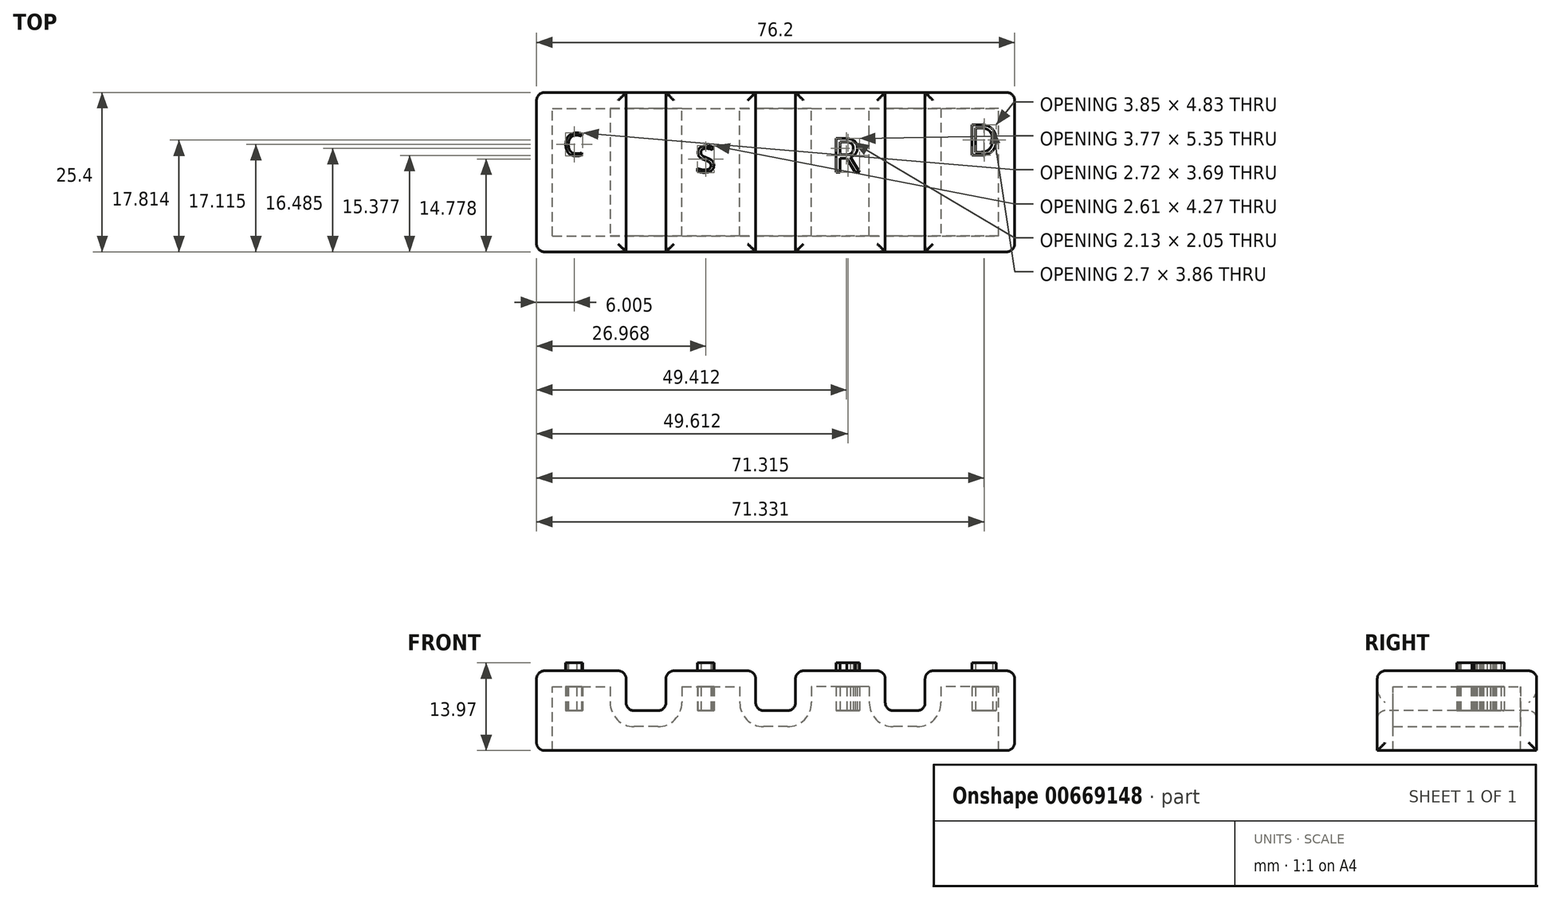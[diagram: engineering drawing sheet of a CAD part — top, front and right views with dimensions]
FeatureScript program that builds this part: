
annotation { "Feature Type Name" : "Feature", "Feature Type Description" : "" }
export const myFeature = defineFeature(function(context is Context, id is Id, definition is map)
    precondition{}
    {
        {
            var Q0;
            Q0=qCreatedBy(makeId("Top.planeOp"),FACE);
            var sketch = newSketch(context, id + "F0", { "sketchPlane" : qUnion([Q0])});
            skLineSegment(sketch, "E0.bottom", {"start": v(-38.1, 12.7) * mm, "end": v(38.1, 12.7) * mm});
            skLineSegment(sketch, "E0.top", {"start": v(-38.1, -12.7) * mm, "end": v(38.1, -12.7) * mm});
            skLineSegment(sketch, "E0.left", {"start": v(-38.1, 12.7) * mm, "end": v(-38.1, -12.7) * mm});
            skLineSegment(sketch, "E0.right", {"start": v(38.1, 12.7) * mm, "end": v(38.1, -12.7) * mm});
            skPoint(sketch, "E0.middle", {"position": v(0, 0) * mm});
            skSolve(sketch);
        }
        {
            var Q0;
            Q0 = qSketchRegion(id + "F0", true);
            extrude(context, id + "F1", {"entities" : qUnion([Q0]), "depth" : 12.7 * mm, "offsetDistance" : 25.4 * mm});
        }
        {
            var Q0;
            Q0=makeQuery(id+"F1.opExtrude","SWEPT_FACE",FACE,{"disambiguationData":[OSD([sQuery(id+"F0.wireOp",EDGE,"E0.top")])]});
            var sketch = newSketch(context, id + "F2", { "sketchPlane" : qUnion([Q0])});
            skLineSegment(sketch, "E1", {"start": v(-38.1, 6.35) * mm, "end": v(38.1, 6.35) * mm, "construction": true});
            skLineSegment(sketch, "E2.bottom", {"start": v(-3.18, 6.35) * mm, "end": v(3.17, 6.35) * mm});
            skLineSegment(sketch, "E2.top", {"start": v(-3.18, 19.05) * mm, "end": v(3.17, 19.05) * mm});
            skLineSegment(sketch, "E2.left", {"start": v(-3.18, 6.35) * mm, "end": v(-3.18, 19.05) * mm});
            skLineSegment(sketch, "E2.right", {"start": v(3.17, 6.35) * mm, "end": v(3.17, 19.05) * mm});
            skPoint(sketch, "E2.middle", {"position": v(0, 12.7) * mm});
            skLineSegment(sketch, "E3.bottom", {"start": v(-23.83, 6.35) * mm, "end": v(-17.48, 6.35) * mm});
            skLineSegment(sketch, "E3.top", {"start": v(-23.83, 19.05) * mm, "end": v(-17.48, 19.05) * mm});
            skLineSegment(sketch, "E3.left", {"start": v(-23.83, 6.35) * mm, "end": v(-23.83, 19.05) * mm});
            skLineSegment(sketch, "E3.right", {"start": v(-17.48, 6.35) * mm, "end": v(-17.48, 19.05) * mm});
            skPoint(sketch, "E3.middle", {"position": v(-20.65, 12.7) * mm});
            skLineSegment(sketch, "E4.bottom", {"start": v(17.48, 6.35) * mm, "end": v(23.83, 6.35) * mm});
            skLineSegment(sketch, "E4.top", {"start": v(17.48, 19.05) * mm, "end": v(23.83, 19.05) * mm});
            skLineSegment(sketch, "E4.left", {"start": v(17.48, 6.35) * mm, "end": v(17.48, 19.05) * mm});
            skLineSegment(sketch, "E4.right", {"start": v(23.83, 6.35) * mm, "end": v(23.83, 19.05) * mm});
            skPoint(sketch, "E4.middle", {"position": v(20.65, 12.7) * mm});
            skSolve(sketch);
        }
        {
            var Q0;
            Q0 = qSketchRegion(id + "F2", true);
            extrude(context, id + "F3", {"entities" : qUnion([Q0]), "operationType" : NewBodyOperationType.REMOVE, "endBound" : BoundingType.THROUGH_ALL, "oppositeDirection" : true, "depth" : 25.4 * mm, "offsetDistance" : 25.4 * mm});
        }
        {
            var Q0;
            {var subQ0=sQuery(id+"F0.wireOp",EDGE,"E0.bottom");var subQ1=sQuery(id+"F0.wireOp",EDGE,"E0.top");var subQ2=sQuery(id+"F0.wireOp",EDGE,"E0.left");Q0=makeQuery(id+"F3.boolean.opBoolean","SPLIT",FACE,{"disambiguationData":[TD([makeQuery(id+"F1.opExtrude","SWEPT_FACE",FACE,{"disambiguationData":[OSD([subQ2])]})])],"derivedFrom":makeQuery(id+"F1.opExtrude","CAP_FACE",FACE,{"disambiguationData":[OSD([subQ0,subQ1,subQ2,sQuery(id+"F0.wireOp",EDGE,"E0.right")])],"isStart":false})});}
            var Q1;
            {var subQ0=sQuery(id+"F0.wireOp",EDGE,"E0.bottom");var subQ1=sQuery(id+"F0.wireOp",EDGE,"E0.top");Q1=makeQuery(id+"F3.boolean.opBoolean","SPLIT",FACE,{"disambiguationData":[TD([makeQuery(id+"F3.opExtrude","SWEPT_FACE",FACE,{"disambiguationData":[OSD([sQuery(id+"F2.wireOp",EDGE,"E2.left")])]})])],"derivedFrom":makeQuery(id+"F1.opExtrude","CAP_FACE",FACE,{"disambiguationData":[OSD([subQ0,subQ1,sQuery(id+"F0.wireOp",EDGE,"E0.left"),sQuery(id+"F0.wireOp",EDGE,"E0.right")])],"isStart":false})});}
            var Q2;
            {var subQ0=sQuery(id+"F0.wireOp",EDGE,"E0.bottom");var subQ1=sQuery(id+"F0.wireOp",EDGE,"E0.top");Q2=makeQuery(id+"F3.boolean.opBoolean","SPLIT",FACE,{"disambiguationData":[TD([makeQuery(id+"F3.opExtrude","SWEPT_FACE",FACE,{"disambiguationData":[OSD([sQuery(id+"F2.wireOp",EDGE,"E2.right")])]})])],"derivedFrom":makeQuery(id+"F1.opExtrude","CAP_FACE",FACE,{"disambiguationData":[OSD([subQ0,subQ1,sQuery(id+"F0.wireOp",EDGE,"E0.left"),sQuery(id+"F0.wireOp",EDGE,"E0.right")])],"isStart":false})});}
            var Q3;
            {var subQ0=sQuery(id+"F0.wireOp",EDGE,"E0.bottom");var subQ1=sQuery(id+"F0.wireOp",EDGE,"E0.right");var subQ2=sQuery(id+"F0.wireOp",EDGE,"E0.top");Q3=makeQuery(id+"F3.boolean.opBoolean","SPLIT",FACE,{"disambiguationData":[TD([makeQuery(id+"F1.opExtrude","SWEPT_FACE",FACE,{"disambiguationData":[OSD([subQ1])]})])],"derivedFrom":makeQuery(id+"F1.opExtrude","CAP_FACE",FACE,{"disambiguationData":[OSD([subQ0,subQ2,sQuery(id+"F0.wireOp",EDGE,"E0.left"),subQ1])],"isStart":false})});}
            var Q4;
            Q4=makeQuery(id+"F3.boolean.opBoolean","COPY",FACE,{"derivedFrom":makeQuery(id+"F3.opExtrude","SWEPT_FACE",FACE,{"disambiguationData":[OSD([sQuery(id+"F2.wireOp",EDGE,"E3.bottom")])]})});
            var Q5;
            Q5=makeQuery(id+"F3.boolean.opBoolean","COPY",FACE,{"derivedFrom":makeQuery(id+"F3.opExtrude","SWEPT_FACE",FACE,{"disambiguationData":[OSD([sQuery(id+"F2.wireOp",EDGE,"E2.bottom")])]})});
            var Q6;
            Q6=makeQuery(id+"F3.boolean.opBoolean","COPY",FACE,{"derivedFrom":makeQuery(id+"F3.opExtrude","SWEPT_FACE",FACE,{"disambiguationData":[OSD([sQuery(id+"F2.wireOp",EDGE,"E4.bottom")])]})});
            var Q7;
            Q7=makeQuery(id+"F1.opExtrude","SWEPT_EDGE",EDGE,{"disambiguationData":[OSD([sQuery(id+"F0.wireOp",EDGE,"E0.bottom"),sQuery(id+"F0.wireOp",EDGE,"E0.right")])]});
            var Q8;
            Q8=makeQuery(id+"F1.opExtrude","SWEPT_FACE",FACE,{"disambiguationData":[OSD([sQuery(id+"F0.wireOp",EDGE,"E0.right")])]});
            var Q9;
            Q9=makeQuery(id+"F1.opExtrude","SWEPT_FACE",FACE,{"disambiguationData":[OSD([sQuery(id+"F0.wireOp",EDGE,"E0.left")])]});
            fillet(context, id + "F4", {"entities" : qUnion([Q0, Q1, Q2, Q3, Q4, Q5, Q6, Q7, Q8, Q9]), "radius" : 1.27 * mm, "tangentPropagation" : true, "allowEdgeOverflow" : false});
        }
        {
            var Q0;
            Q0=makeQuery(id+"F1.opExtrude","CAP_FACE",FACE,{"disambiguationData":[OSD([sQuery(id+"F0.wireOp",EDGE,"E0.bottom"),sQuery(id+"F0.wireOp",EDGE,"E0.top"),sQuery(id+"F0.wireOp",EDGE,"E0.left"),sQuery(id+"F0.wireOp",EDGE,"E0.right")])],"isStart":true});
            shell(context, id + "F5", {"entities" : qUnion([Q0]), "thickness" : 2.54 * mm});
        }
        {
            var Q0;
            Q0=makeQuery(id+"F3.boolean.opBoolean","COPY",FACE,{"derivedFrom":makeQuery(id+"F3.opExtrude","SWEPT_FACE",FACE,{"disambiguationData":[OSD([sQuery(id+"F2.wireOp",EDGE,"E3.bottom")])]})});
            var sketch = newSketch(context, id + "F6", { "sketchPlane" : qUnion([Q0])});
            skText(sketch, "E5", { "text": "C", "fontName": "OpenSans-Regular.ttf"});
            skText(sketch, "E6", { "text": "S", "fontName": "OpenSans-Regular.ttf"});
            skText(sketch, "E7", { "text": "R\n", "fontName": "OpenSans-Regular.ttf"});
            skText(sketch, "E8", { "text": "D", "fontName": "OpenSans-Regular.ttf"});
            skPoint(sketch, "E8.firstSnap0", {"position": v(8.89, 2.7) * mm});
            const initialGuessF6  = {"E5": [-0.03376, 0.00262, 1, 0, 0.00362], "E6": [-0.01274, 0, 1, 0, 0.00419], "E7": [0.00889, 0, 1, 0, 0.0054], "E8": [0.03064, 0.0027, 1, 0, 0.00487]};
            skSetInitialGuess(sketch, initialGuessF6);
            skSolve(sketch);
        }
        {
            var Q0;
            Q0 = qSketchRegion(id + "F6", true);
            var Q1;
            Q1 = qSketchRegion(id + "FjAx4vn2NLacunU_1", true);
            extrude(context, id + "F7", {"entities" : qUnion([Q0, Q1]), "operationType" : NewBodyOperationType.ADD, "depth" : 7.62 * mm, "offsetDistance" : 25.4 * mm});
        }
    });
